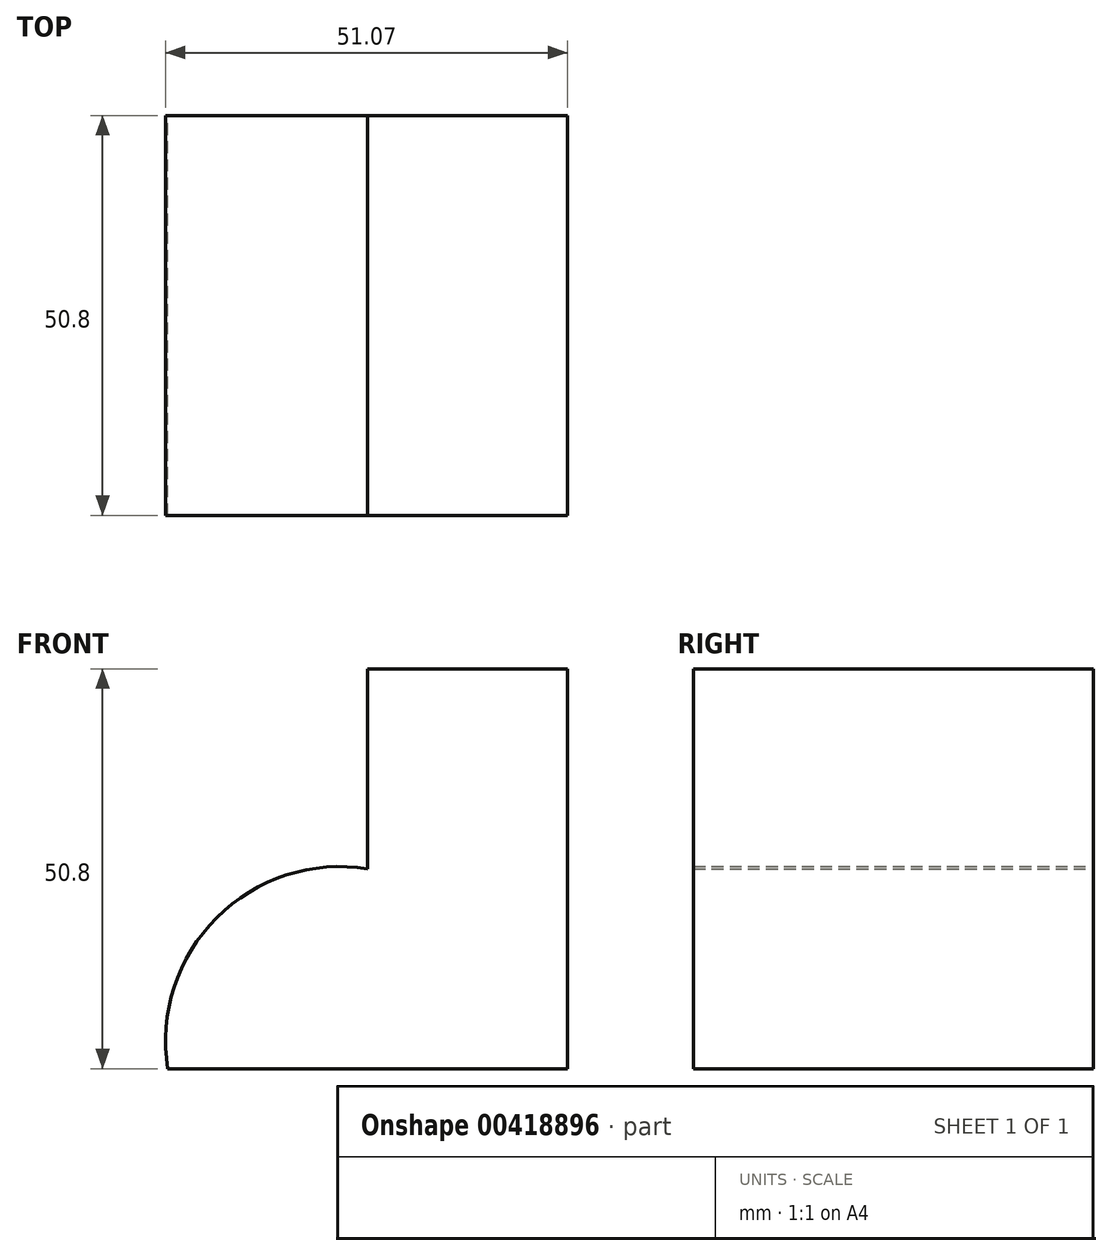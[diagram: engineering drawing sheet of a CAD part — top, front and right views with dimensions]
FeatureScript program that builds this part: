
annotation { "Feature Type Name" : "Feature", "Feature Type Description" : "" }
export const myFeature = defineFeature(function(context is Context, id is Id, definition is map)
    precondition{}
    {
        {
            var Q0;
            Q0=qCreatedBy(makeId("Front.planeOp"),FACE);
            var sketch = newSketch(context, id + "F0", { "sketchPlane" : qUnion([Q0])});
            skLineSegment(sketch, "E0.bottom", {"start": v(0, 0) * mm, "end": v(-25.4, 0) * mm});
            skLineSegment(sketch, "E0.top", {"start": v(0, 25.4) * mm, "end": v(-25.4, 25.4) * mm});
            skLineSegment(sketch, "E0.left", {"start": v(0, 0) * mm, "end": v(0, 25.4) * mm});
            skLineSegment(sketch, "E0.right", {"start": v(-25.4, 0) * mm, "end": v(-25.4, 25.4) * mm});
            skLineSegment(sketch, "E1", {"start": v(0, 0) * mm, "end": v(0, -25.4) * mm});
            skLineSegment(sketch, "E2", {"start": v(0, -25.4) * mm, "end": v(-50.8, -25.4) * mm});
            skArc(sketch, "E3", {"start": v(-25.4, 0) * mm, "mid": v(-44.57, -6.23) * mm, "end": v(-50.8, -25.4) * mm});
            skSolve(sketch);
        }
        {
            var Q0;
            Q0 = qSketchRegion(id + "F0", true);
            extrude(context, id + "F1", {"entities" : qUnion([Q0]), "depth" : 50.8 * mm});
        }
    });
